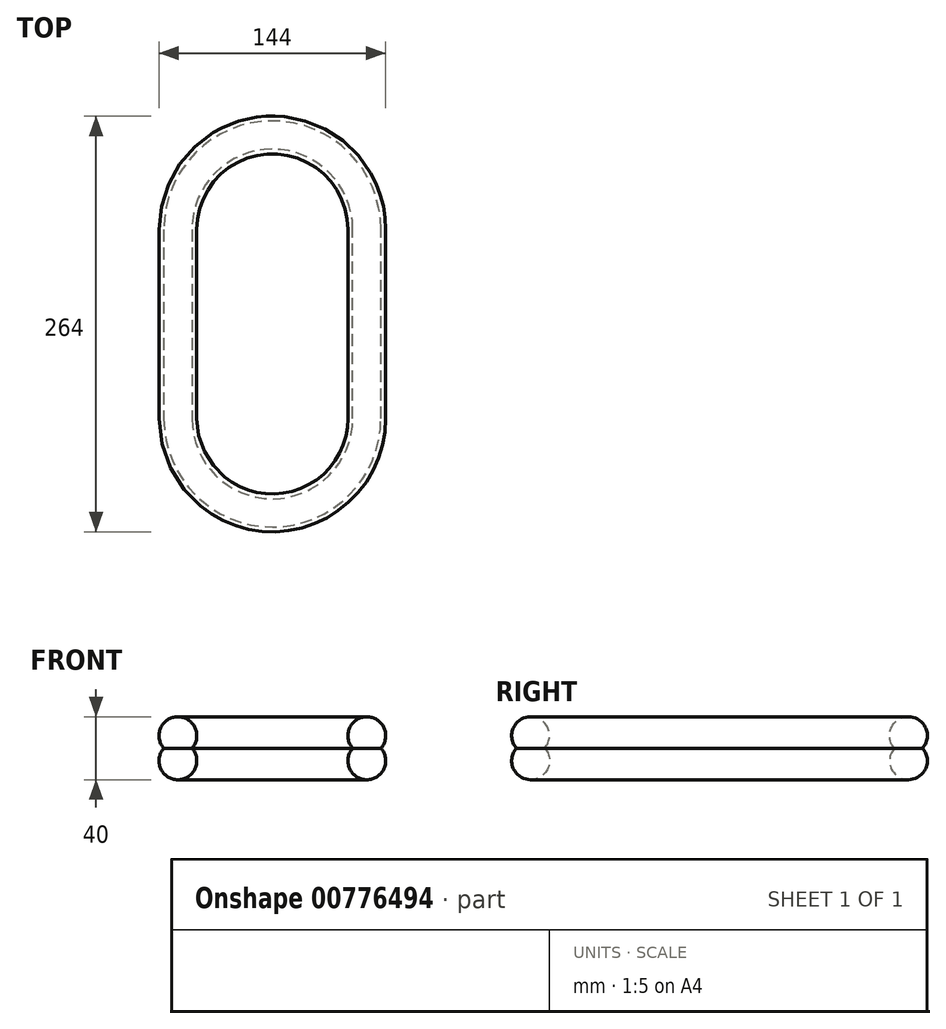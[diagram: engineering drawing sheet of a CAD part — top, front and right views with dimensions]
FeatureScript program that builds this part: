
annotation { "Feature Type Name" : "Feature", "Feature Type Description" : "" }
export const myFeature = defineFeature(function(context is Context, id is Id, definition is map)
    precondition{}
    {
        {
            var Q0;
            Q0=qCreatedBy(makeId("Front.planeOp"),FACE);
            var sketch = newSketch(context, id + "F0", { "sketchPlane" : qUnion([Q0])});
            skArc(sketch, "E0", {"start": v(-68.94, 0) * mm, "mid": v(-60, -20) * mm, "end": v(-51.06, 0) * mm});
            skArc(sketch, "E1", {"start": v(-51.06, 0) * mm, "mid": v(-60, 20) * mm, "end": v(-68.94, 0) * mm});
            skSolve(sketch);
        }
        {
            var Q0;
            Q0=qCreatedBy(makeId("Top.planeOp"),FACE);
            var sketch = newSketch(context, id + "F1", { "sketchPlane" : qUnion([Q0])});
            skLineSegment(sketch, "E2", {"start": v(-60, -60) * mm, "end": v(-60, 60) * mm});
            skArc(sketch, "E3", {"start": v(60, 60) * mm, "mid": v(0, 120) * mm, "end": v(-60, 60) * mm});
            skLineSegment(sketch, "E4", {"start": v(60, 60) * mm, "end": v(60, -60) * mm});
            skArc(sketch, "E5", {"start": v(-60, -60) * mm, "mid": v(0, -120) * mm, "end": v(60, -60) * mm});
            skSolve(sketch);
        }
        {
            var Q0;
            Q0=makeQuery(id+"F0.imprint","IMPRINT",FACE,{"disambiguationData":[TD([[makeQuery(id+"F0.imprint","IMPRINT",EDGE,{"derivedFrom":sQuery(id+"F0.wireOp",EDGE,"E0")}),1.0]])]});
            var Q1;
            Q1=sQuery(id+"F1.wireOp",EDGE,"E2");
            var Q2;
            Q2=sQuery(id+"F1.wireOp",EDGE,"E3");
            var Q3;
            Q3=sQuery(id+"F1.wireOp",EDGE,"E4");
            var Q4;
            Q4=sQuery(id+"F1.wireOp",EDGE,"E5");
            sweep(context, id + "F2", {"profiles" : qUnion([Q0]), "path" : qUnion([Q1, Q2, Q3, Q4])});
        }
    });
